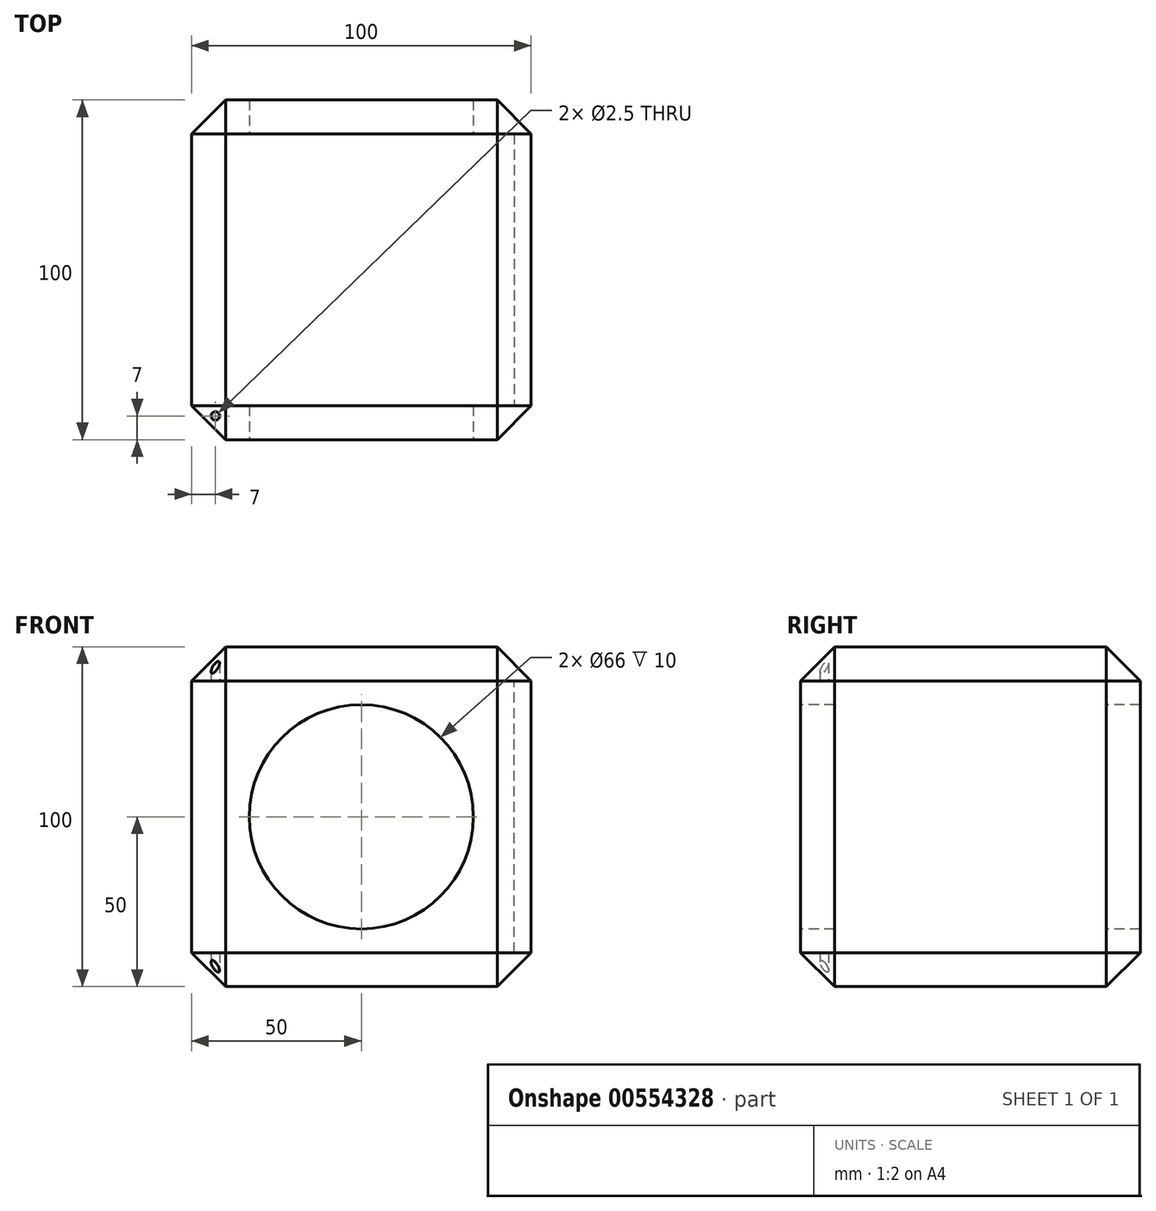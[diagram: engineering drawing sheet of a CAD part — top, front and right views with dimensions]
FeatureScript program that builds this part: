
annotation { "Feature Type Name" : "Feature", "Feature Type Description" : "" }
export const myFeature = defineFeature(function(context is Context, id is Id, definition is map)
    precondition{}
    {
        {
            var Q0;
            Q0=qCreatedBy(makeId("Top.planeOp"),FACE);
            var sketch = newSketch(context, id + "F0", { "sketchPlane" : qUnion([Q0])});
            skLineSegment(sketch, "E0.bottom", {"start": v(50, -50) * mm, "end": v(-50, -50) * mm});
            skLineSegment(sketch, "E0.top", {"start": v(50, 50) * mm, "end": v(-50, 50) * mm});
            skLineSegment(sketch, "E0.left", {"start": v(50, -50) * mm, "end": v(50, 50) * mm});
            skLineSegment(sketch, "E0.right", {"start": v(-50, -50) * mm, "end": v(-50, 50) * mm});
            skPoint(sketch, "E0.middle", {"position": v(0, 0) * mm});
            skSolve(sketch);
        }
        {
            var Q0;
            Q0 = qSketchRegion(id + "F0", true);
            extrude(context, id + "F1", {"entities" : qUnion([Q0]), "endBound" : BoundingType.SYMMETRIC, "depth" : 100 * mm, "offsetDistance" : 25 * mm});
        }
        {
            var Q0;
            Q0=makeQuery(id+"F1.opExtrude","SWEPT_EDGE",EDGE,{"disambiguationData":[OSD([sQuery(id+"F0.wireOp",EDGE,"E0.top"),sQuery(id+"F0.wireOp",EDGE,"E0.right")])]});
            var Q1;
            Q1=makeQuery(id+"F1.opExtrude","CAP_EDGE",EDGE,{"disambiguationData":[OSD([sQuery(id+"F0.wireOp",EDGE,"E0.top")])],"isStart":false});
            var Q2;
            Q2=makeQuery(id+"F1.opExtrude","CAP_EDGE",EDGE,{"disambiguationData":[OSD([sQuery(id+"F0.wireOp",EDGE,"E0.top")])],"isStart":true});
            var Q3;
            Q3=makeQuery(id+"F1.opExtrude","SWEPT_EDGE",EDGE,{"disambiguationData":[OSD([sQuery(id+"F0.wireOp",EDGE,"E0.top"),sQuery(id+"F0.wireOp",EDGE,"E0.left")])]});
            var Q4;
            Q4=makeQuery(id+"F1.opExtrude","CAP_EDGE",EDGE,{"disambiguationData":[OSD([sQuery(id+"F0.wireOp",EDGE,"E0.right")])],"isStart":true});
            var Q5;
            Q5=makeQuery(id+"F1.opExtrude","SWEPT_EDGE",EDGE,{"disambiguationData":[OSD([sQuery(id+"F0.wireOp",EDGE,"E0.bottom"),sQuery(id+"F0.wireOp",EDGE,"E0.right")])]});
            var Q6;
            Q6=makeQuery(id+"F1.opExtrude","CAP_EDGE",EDGE,{"disambiguationData":[OSD([sQuery(id+"F0.wireOp",EDGE,"E0.right")])],"isStart":false});
            var Q7;
            Q7=makeQuery(id+"F1.opExtrude","CAP_EDGE",EDGE,{"disambiguationData":[OSD([sQuery(id+"F0.wireOp",EDGE,"E0.bottom")])],"isStart":true});
            var Q8;
            Q8=makeQuery(id+"F1.opExtrude","CAP_EDGE",EDGE,{"disambiguationData":[OSD([sQuery(id+"F0.wireOp",EDGE,"E0.bottom")])],"isStart":false});
            var Q9;
            Q9=makeQuery(id+"F1.opExtrude","SWEPT_EDGE",EDGE,{"disambiguationData":[OSD([sQuery(id+"F0.wireOp",EDGE,"E0.bottom"),sQuery(id+"F0.wireOp",EDGE,"E0.left")])]});
            var Q10;
            Q10=makeQuery(id+"F1.opExtrude","CAP_EDGE",EDGE,{"disambiguationData":[OSD([sQuery(id+"F0.wireOp",EDGE,"E0.left")])],"isStart":true});
            var Q11;
            Q11=makeQuery(id+"F1.opExtrude","CAP_EDGE",EDGE,{"disambiguationData":[OSD([sQuery(id+"F0.wireOp",EDGE,"E0.left")])],"isStart":false});
            chamfer(context, id + "F2", {"entities" : qUnion([Q0, Q1, Q2, Q3, Q4, Q5, Q6, Q7, Q8, Q9, Q10, Q11]), "width" : 10 * mm, "tangentPropagation" : true});
        }
        {
            var Q0;
            Q0=makeQuery(id+"F1.opExtrude","SWEPT_FACE",FACE,{"disambiguationData":[OSD([sQuery(id+"F0.wireOp",EDGE,"E0.right")])]});
            extrude(context, id + "F3", {"entities" : qUnion([Q0]), "operationType" : NewBodyOperationType.REMOVE, "oppositeDirection" : true, "depth" : 5 * mm, "offsetDistance" : 25 * mm});
        }
        {
            var Q0;
            Q0=makeQuery(id+"F3.boolean.opBoolean","COPY",FACE,{"derivedFrom":makeQuery(id+"F3.opExtrude","CAP_FACE",FACE,{"disambiguationData":[OSD([sQuery(id+"F0.wireOp",EDGE,"E0.right")])],"isStart":false})});
            extrude(context, id + "F4", {"entities" : qUnion([Q0]), "operationType" : NewBodyOperationType.REMOVE, "oppositeDirection" : true, "depth" : 90 * mm, "offsetDistance" : 25 * mm});
        }
        {
            var Q0;
            {var subQ0=sQuery(id+"F0.wireOp",EDGE,"E0.right");var subQ1=sQuery(id+"F0.wireOp",EDGE,"E0.bottom");Q0=makeQuery(id+"F4.boolean.opBoolean","MERGE",FACE,{"derivedFrom":[makeQuery(id+"F3.boolean.opBoolean","COPY",FACE,{"derivedFrom":makeQuery(id+"F3.opExtrude","SWEPT_FACE",FACE,{"disambiguationData":[OSD([subQ1,subQ0])]})}),makeQuery(id+"F4.opExtrude","SWEPT_FACE",FACE,{"disambiguationData":[OSD([subQ1,subQ0])]})]});}
            var sketch = newSketch(context, id + "F5", { "sketchPlane" : qUnion([Q0])});
            skLineSegment(sketch, "E1", {"start": v(40, 40) * mm, "end": v(40, -40) * mm});
            skSolve(sketch);
        }
        {
            var Q0;
            {var subQ0=sQuery(id+"F5.wireOp",EDGE,"E1");Q0=makeQuery(id+"F5.imprint","IMPRINT",FACE,{"disambiguationData":[TD([[makeQuery(id+"F5.imprint","IMPRINT",EDGE,{"derivedFrom":subQ0}),1.0]])]});}
            extrude(context, id + "F6", {"entities" : qUnion([Q0]), "operationType" : NewBodyOperationType.REMOVE, "oppositeDirection" : true, "depth" : 25 * mm, "offsetDistance" : 25 * mm});
        }
        {
            var Q0;
            {var subQ0=sQuery(id+"F0.wireOp",EDGE,"E0.right");var subQ1=makeQuery(id+"F1.opExtrude","SWEPT_FACE",FACE,{"disambiguationData":[OSD([subQ0])]});var subQ2=makeQuery(id+"F1.opExtrude","CAP_EDGE",EDGE,{"disambiguationData":[OSD([subQ0])],"isStart":false});var subQ3=sQuery(id+"F0.wireOp",EDGE,"E0.bottom");var subQ4=makeQuery(id+"F1.opExtrude","SWEPT_EDGE",EDGE,{"disambiguationData":[OSD([subQ3,subQ0])]});var subQ5=makeQuery(id+"F2.opChamfer","BLEND_VERTEX",VERTEX,{"blendedFrom":[makeQuery(id+"F1.opExtrude","CAP_VERTEX",VERTEX,{"disambiguationData":[OSD([subQ3,subQ0])],"isStart":false}),subQ4,subQ2,subQ1],"blendedInto":[subQ1]});var subQ6=makeQuery(id+"F4.boolean.opBoolean","MERGE",EDGE,{"derivedFrom":[makeQuery(id+"F3.boolean.opBoolean","COPY",EDGE,{"derivedFrom":makeQuery(id+"F3.opExtrude","SWEPT_EDGE",EDGE,{"disambiguationData":[OSD([subQ3,subQ0]),TDD([subQ5])]})}),makeQuery(id+"F4.opExtrude","SWEPT_EDGE",EDGE,{"disambiguationData":[OSD([subQ3,subQ0]),TDD([makeQuery(id+"F3.boolean.opBoolean","COPY",VERTEX,{"derivedFrom":makeQuery(id+"F3.opExtrude","CAP_VERTEX",VERTEX,{"disambiguationData":[OSD([subQ3,subQ0]),TDD([subQ5])],"isStart":false})})])]})]});var subQ7=makeQuery(id+"F2.opChamfer","BLEND_EDGE",EDGE,{"blendedFrom":[subQ2,subQ1],"blendedInto":[subQ1]});Q0=makeQuery(id+"F6.boolean.opBoolean","MERGE",FACE,{"derivedFrom":[makeQuery(id+"F4.boolean.opBoolean","MERGE",FACE,{"derivedFrom":[makeQuery(id+"F3.boolean.opBoolean","COPY",FACE,{"derivedFrom":makeQuery(id+"F3.opExtrude","SWEPT_FACE",FACE,{"disambiguationData":[OSD([subQ0]),TDD([subQ7])]})}),makeQuery(id+"F4.opExtrude","SWEPT_FACE",FACE,{"disambiguationData":[OSD([subQ0]),TDD([makeQuery(id+"F3.boolean.opBoolean","COPY",EDGE,{"derivedFrom":makeQuery(id+"F3.opExtrude","CAP_EDGE",EDGE,{"disambiguationData":[OSD([subQ0]),TDD([subQ7])],"isStart":false})})])]})]}),makeQuery(id+"F6.opExtrude","SWEPT_FACE",FACE,{"disambiguationData":[OSD([subQ3,subQ0]),TDD([makeQuery(id+"F5.imprint","IMPRINT",EDGE,{"disambiguationData":[TD([[makeQuery(id+"F5.imprint","INTERSECT",VERTEX,{"derivedFrom":[subQ6,sQuery(id+"F5.wireOp",EDGE,"E1")]}),-1.0]])],"derivedFrom":subQ6})])]})]});}
            var sketch = newSketch(context, id + "F7", { "sketchPlane" : qUnion([Q0])});
            skLineSegment(sketch, "E2", {"start": v(-50, 40) * mm, "end": v(-40, 40) * mm});
            skCircle(sketch, "E3", {"center": v(-43, 43) * mm, "radius": 1.25 * mm});
            skSolve(sketch);
        }
        {
            var Q0;
            Q0 = qSketchRegion(id + "F7", true);
            extrude(context, id + "F8", {"entities" : qUnion([Q0]), "operationType" : NewBodyOperationType.REMOVE, "endBound" : BoundingType.SYMMETRIC, "oppositeDirection" : true, "depth" : 200 * mm, "offsetDistance" : 25 * mm});
        }
        {
            var Q0;
            Q0=makeQuery(id+"F1.opExtrude","SWEPT_FACE",FACE,{"disambiguationData":[OSD([sQuery(id+"F0.wireOp",EDGE,"E0.bottom")])]});
            var sketch = newSketch(context, id + "F9", { "sketchPlane" : qUnion([Q0])});
            skCircle(sketch, "E4", {"center": v(0, 0) * mm, "radius": 33 * mm});
            skSolve(sketch);
        }
        {
            var Q0;
            Q0 = qSketchRegion(id + "F9", true);
            extrude(context, id + "F10", {"entities" : qUnion([Q0]), "operationType" : NewBodyOperationType.REMOVE, "oppositeDirection" : true, "depth" : 150 * mm, "offsetDistance" : 25 * mm});
        }
    });
